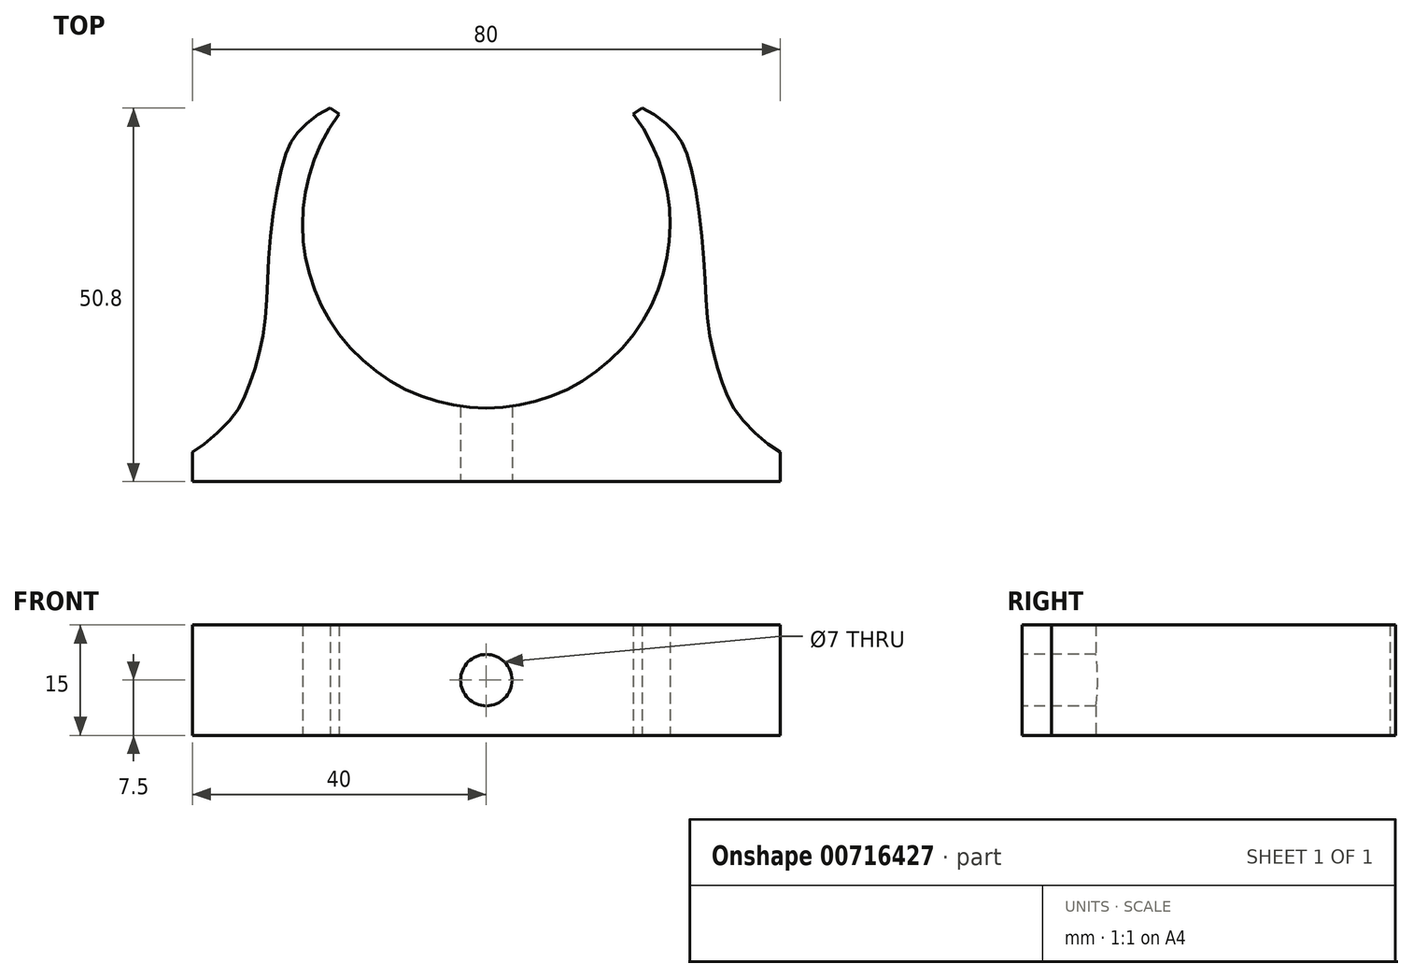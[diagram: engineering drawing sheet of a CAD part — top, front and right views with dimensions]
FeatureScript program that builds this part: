
annotation { "Feature Type Name" : "Feature", "Feature Type Description" : "" }
export const myFeature = defineFeature(function(context is Context, id is Id, definition is map)
    precondition{}
    {
        {
            var Q0;
            Q0=qCreatedBy(makeId("Top.planeOp"),FACE);
            var sketch = newSketch(context, id + "F0", { "sketchPlane" : qUnion([Q0])});
            skArc(sketch, "E0", {"start": v(0, 10) * mm, "mid": v(22.36, 23.82) * mm, "end": v(20, 50) * mm});
            skLineSegment(sketch, "E1", {"start": v(44.02, 50) * mm, "end": v(-32.67, 50) * mm, "construction": true});
            skLineSegment(sketch, "E2", {"start": v(0, 71.16) * mm, "end": v(0, -30.89) * mm, "construction": true});
            skLineSegment(sketch, "E3", {"start": v(20, 50) * mm, "end": v(21.21, 50.8) * mm});
            skLineSegment(sketch, "E4", {"start": v(0, 10) * mm, "end": v(0, 0) * mm});
            skLineSegment(sketch, "E5", {"start": v(0, 0) * mm, "end": v(40, 0) * mm});
            skLineSegment(sketch, "E6", {"start": v(40, 0) * mm, "end": v(40, 4) * mm});
            skFitSpline(sketch, "E7", {"points": [v(21.21, 50.8) * mm, v(25.42, 47.75) * mm, v(27.46, 44.08) * mm, v(29.5, 31.52) * mm, v(30.22, 20.9) * mm, v(32.05, 13.65) * mm, v(34.6, 8.65) * mm, v(40, 4) * mm], "startDerivative": vector(37.67, -14.8) * mm, "endDerivative": vector(34.37, -20.6) * mm});
            skLineSegment(sketch, "E8.MirrorCS", {"start": v(-20, 50) * mm, "end": v(-21.21, 50.8) * mm});
            skArc(sketch, "E9.MirrorCS", {"start": v(0, 10) * mm, "mid": v(-22.36, 23.82) * mm, "end": v(-20, 50) * mm});
            skFitSpline(sketch, "E10.MirrorCS", {"points": [v(-21.21, 50.8) * mm, v(-25.42, 47.75) * mm, v(-27.46, 44.08) * mm, v(-29.5, 31.52) * mm, v(-30.22, 20.9) * mm, v(-32.05, 13.65) * mm, v(-34.6, 8.65) * mm, v(-40, 4) * mm], "startDerivative": vector(-37.67, -14.8) * mm, "endDerivative": vector(-34.37, -20.6) * mm});
            skLineSegment(sketch, "E11.MirrorCS", {"start": v(-40, 0) * mm, "end": v(-40, 4) * mm});
            skLineSegment(sketch, "E12.MirrorCS", {"start": v(0, 0) * mm, "end": v(-40, 0) * mm});
            skSolve(sketch);
        }
        {
            var Q0;
            Q0 = qSketchRegion(id + "F0", true);
            extrude(context, id + "F1", {"entities" : qUnion([Q0]), "depth" : 15 * mm, "offsetDistance" : 25 * mm});
        }
        {
            var Q0;
            Q0=makeQuery(id+"F1.opExtrude","SWEPT_FACE",FACE,{"disambiguationData":[OSD([sQuery(id+"F0.wireOp",EDGE,"E5"),sQuery(id+"F0.wireOp",EDGE,"E12.MirrorCS")])]});
            var sketch = newSketch(context, id + "F2", { "sketchPlane" : qUnion([Q0])});
            skCircle(sketch, "E13", {"center": v(0, 7.5) * mm, "radius": 3.5 * mm});
            skPoint(sketch, "E13.centerSnap0", {"position": v(-40, 7.5) * mm});
            skSolve(sketch);
        }
        {
            var Q0;
            Q0 = qSketchRegion(id + "F2", true);
            extrude(context, id + "F3", {"entities" : qUnion([Q0]), "operationType" : NewBodyOperationType.REMOVE, "oppositeDirection" : true, "depth" : 25 * mm, "offsetDistance" : 25 * mm});
        }
    });
